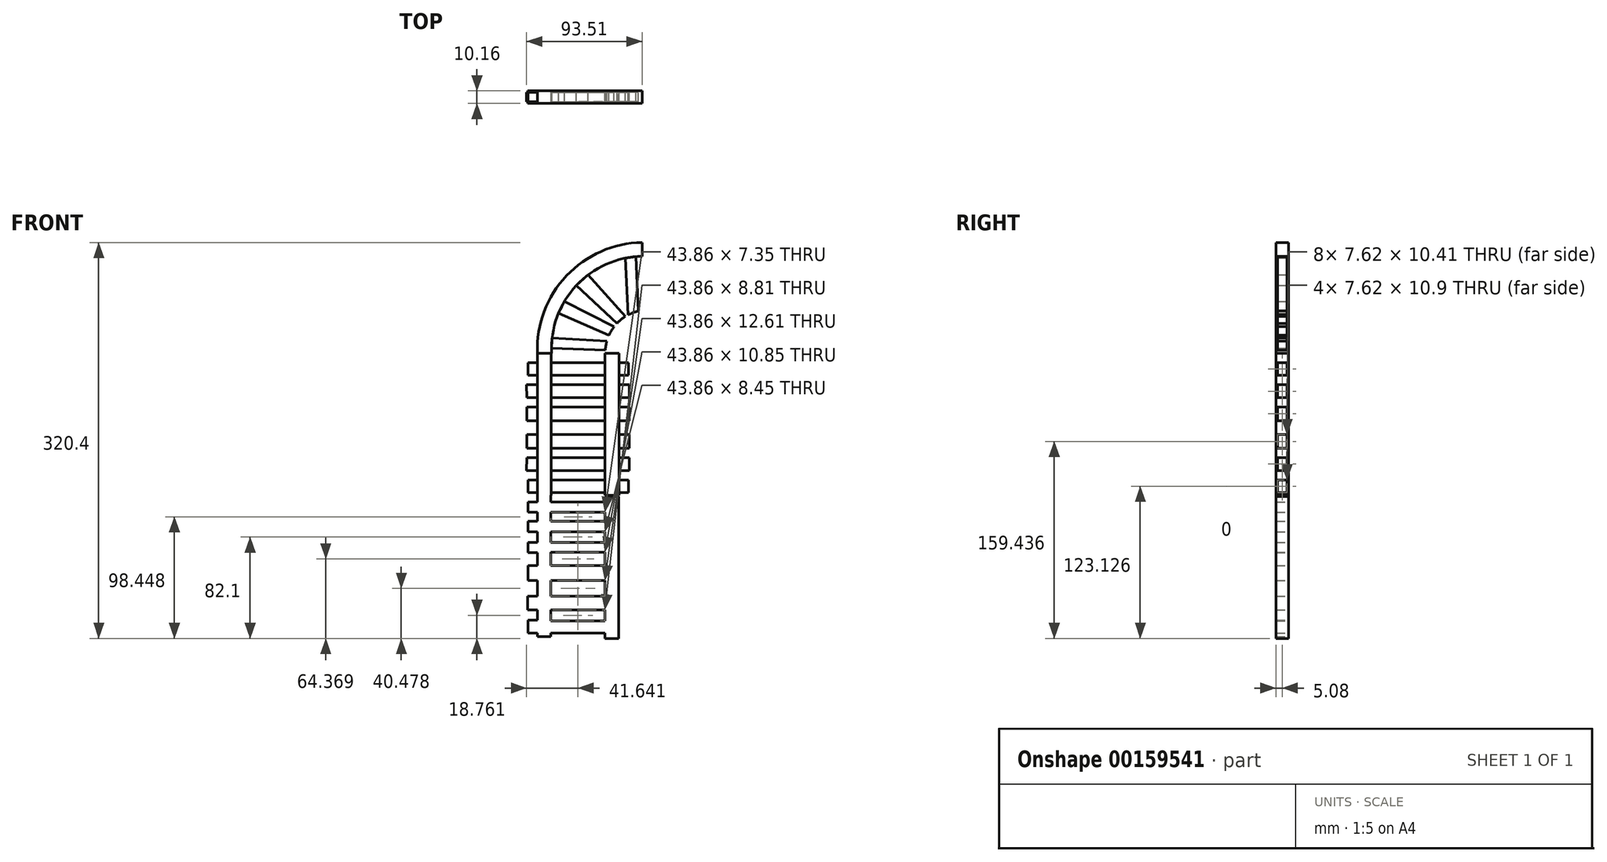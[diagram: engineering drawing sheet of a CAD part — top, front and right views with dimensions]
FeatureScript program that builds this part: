
annotation { "Feature Type Name" : "Feature", "Feature Type Description" : "" }
export const myFeature = defineFeature(function(context is Context, id is Id, definition is map)
    precondition{}
    {
        {
            var Q0;
            Q0=qCreatedBy(makeId("Front.planeOp"),FACE);
            var sketch = newSketch(context, id + "F0", { "sketchPlane" : qUnion([Q0])});
            skLineSegment(sketch, "E0", {"start": v(-21.84, 60.28) * mm, "end": v(-21.84, -54.78) * mm});
            skLineSegment(sketch, "E1", {"start": v(-21.84, -54.78) * mm, "end": v(-33.02, -54.78) * mm});
            skLineSegment(sketch, "E2", {"start": v(-33.02, -54.78) * mm, "end": v(-33.02, 60.28) * mm});
            skLineSegment(sketch, "E3", {"start": v(-33.02, 60.28) * mm, "end": v(-21.84, 60.28) * mm});
            skLineSegment(sketch, "E4.MirrorCS", {"start": v(21.84, 60.28) * mm, "end": v(21.84, -54.78) * mm});
            skLineSegment(sketch, "E5.MirrorCS", {"start": v(33.02, -54.78) * mm, "end": v(33.02, 60.28) * mm});
            skLineSegment(sketch, "E6.MirrorCS", {"start": v(33.02, 60.28) * mm, "end": v(21.84, 60.28) * mm});
            skLineSegment(sketch, "E7.MirrorCS", {"start": v(21.84, -54.78) * mm, "end": v(33.02, -54.78) * mm});
            skLineSegment(sketch, "E8", {"start": v(-40.64, 42.25) * mm, "end": v(40.64, 42.25) * mm});
            skLineSegment(sketch, "E9", {"start": v(40.64, 42.25) * mm, "end": v(40.64, 52.66) * mm});
            skLineSegment(sketch, "E10", {"start": v(40.64, 52.66) * mm, "end": v(-40.64, 52.66) * mm});
            skLineSegment(sketch, "E11", {"start": v(-40.64, 52.66) * mm, "end": v(-40.64, 42.25) * mm});
            skLineSegment(sketch, "E12", {"start": v(-41.74, 34.63) * mm, "end": v(41.35, 34.63) * mm});
            skLineSegment(sketch, "E13", {"start": v(41.35, 34.63) * mm, "end": v(41.35, 24.21) * mm});
            skLineSegment(sketch, "E14", {"start": v(41.35, 24.21) * mm, "end": v(-41.51, 24.21) * mm});
            skLineSegment(sketch, "E15", {"start": v(-41.51, 24.21) * mm, "end": v(-41.74, 34.63) * mm});
            skLineSegment(sketch, "E16", {"start": v(-33.02, 16.6) * mm, "end": v(-41.51, 16.6) * mm});
            skLineSegment(sketch, "E17", {"start": v(-41.51, 16.6) * mm, "end": v(-41.51, 5.7) * mm});
            skLineSegment(sketch, "E18", {"start": v(-41.51, 5.7) * mm, "end": v(41.4, 5.7) * mm});
            skLineSegment(sketch, "E19", {"start": v(41.4, 5.7) * mm, "end": v(41.4, 16.6) * mm});
            skLineSegment(sketch, "E20", {"start": v(-33.02, 16.6) * mm, "end": v(41.4, 16.6) * mm});
            skLineSegment(sketch, "E21.MirrorCS", {"start": v(-41.51, -5.7) * mm, "end": v(41.4, -5.7) * mm});
            skLineSegment(sketch, "E22.MirrorCS", {"start": v(-41.51, -16.6) * mm, "end": v(-41.51, -5.7) * mm});
            skLineSegment(sketch, "E23.MirrorCS", {"start": v(41.4, -5.7) * mm, "end": v(41.4, -16.6) * mm});
            skLineSegment(sketch, "E24.MirrorCS", {"start": v(-33.02, -16.6) * mm, "end": v(41.4, -16.6) * mm});
            skLineSegment(sketch, "E25.MirrorCS", {"start": v(-33.02, -16.6) * mm, "end": v(-41.51, -16.6) * mm});
            skLineSegment(sketch, "E26.MirrorCS", {"start": v(41.35, -24.21) * mm, "end": v(-41.51, -24.21) * mm});
            skLineSegment(sketch, "E27.MirrorCS", {"start": v(-41.74, -34.63) * mm, "end": v(41.35, -34.63) * mm});
            skLineSegment(sketch, "E28.MirrorCS", {"start": v(-41.51, -24.21) * mm, "end": v(-41.74, -34.63) * mm});
            skLineSegment(sketch, "E29.MirrorCS", {"start": v(41.35, -34.63) * mm, "end": v(41.35, -24.21) * mm});
            skLineSegment(sketch, "E30.MirrorCS", {"start": v(40.64, -42.25) * mm, "end": v(40.64, -52.66) * mm});
            skLineSegment(sketch, "E31.MirrorCS", {"start": v(40.64, -52.66) * mm, "end": v(-40.64, -52.66) * mm});
            skLineSegment(sketch, "E32.MirrorCS", {"start": v(-40.64, -42.25) * mm, "end": v(40.64, -42.25) * mm});
            skLineSegment(sketch, "E33.MirrorCS", {"start": v(-40.64, -52.66) * mm, "end": v(-40.64, -42.25) * mm});
            skSolve(sketch);
        }
        {
            var Q0;
            {var subQ0=sQuery(id+"F0.wireOp",EDGE,"E3");Q0=makeQuery(id+"F0.imprint","IMPRINT",FACE,{"disambiguationData":[TD([[makeQuery(id+"F0.imprint","IMPRINT",EDGE,{"derivedFrom":subQ0}),-1.0]])]});}
            var Q1;
            {var subQ0=sQuery(id+"F0.wireOp",EDGE,"E10");var subQ1=sQuery(id+"F0.wireOp",EDGE,"E0");var subQ2=makeQuery(id+"F0.imprint","INTERSECT",VERTEX,{"derivedFrom":[subQ1,subQ0]});Q1=makeQuery(id+"F0.imprint","IMPRINT",FACE,{"disambiguationData":[TD([[makeQuery(id+"F0.imprint","IMPRINT",EDGE,{"disambiguationData":[TD([[subQ2,-1.0]])],"derivedFrom":subQ1}),-1.0]])]});}
            var Q2;
            {var subQ0=sQuery(id+"F0.wireOp",EDGE,"E8");var subQ1=sQuery(id+"F0.wireOp",EDGE,"E0");var subQ2=makeQuery(id+"F0.imprint","INTERSECT",VERTEX,{"derivedFrom":[subQ1,subQ0]});Q2=makeQuery(id+"F0.imprint","IMPRINT",FACE,{"disambiguationData":[TD([[makeQuery(id+"F0.imprint","IMPRINT",EDGE,{"disambiguationData":[TD([[subQ2,-1.0]])],"derivedFrom":subQ1}),-1.0]])]});}
            var Q3;
            {var subQ0=sQuery(id+"F0.wireOp",EDGE,"E12");var subQ1=sQuery(id+"F0.wireOp",EDGE,"E0");var subQ2=makeQuery(id+"F0.imprint","INTERSECT",VERTEX,{"derivedFrom":[subQ1,subQ0]});Q3=makeQuery(id+"F0.imprint","IMPRINT",FACE,{"disambiguationData":[TD([[makeQuery(id+"F0.imprint","IMPRINT",EDGE,{"disambiguationData":[TD([[subQ2,-1.0]])],"derivedFrom":subQ1}),-1.0]])]});}
            var Q4;
            {var subQ0=sQuery(id+"F0.wireOp",EDGE,"E14");var subQ1=sQuery(id+"F0.wireOp",EDGE,"E0");var subQ2=makeQuery(id+"F0.imprint","INTERSECT",VERTEX,{"derivedFrom":[subQ1,subQ0]});Q4=makeQuery(id+"F0.imprint","IMPRINT",FACE,{"disambiguationData":[TD([[makeQuery(id+"F0.imprint","IMPRINT",EDGE,{"disambiguationData":[TD([[subQ2,-1.0]])],"derivedFrom":subQ1}),-1.0]])]});}
            var Q5;
            {var subQ0=sQuery(id+"F0.wireOp",EDGE,"E20");var subQ1=sQuery(id+"F0.wireOp",EDGE,"E0");var subQ2=makeQuery(id+"F0.imprint","INTERSECT",VERTEX,{"derivedFrom":[subQ1,subQ0]});Q5=makeQuery(id+"F0.imprint","IMPRINT",FACE,{"disambiguationData":[TD([[makeQuery(id+"F0.imprint","IMPRINT",EDGE,{"disambiguationData":[TD([[subQ2,-1.0]])],"derivedFrom":subQ1}),-1.0]])]});}
            var Q6;
            {var subQ0=sQuery(id+"F0.wireOp",EDGE,"E18");var subQ1=sQuery(id+"F0.wireOp",EDGE,"E0");var subQ2=makeQuery(id+"F0.imprint","INTERSECT",VERTEX,{"derivedFrom":[subQ1,subQ0]});Q6=makeQuery(id+"F0.imprint","IMPRINT",FACE,{"disambiguationData":[TD([[makeQuery(id+"F0.imprint","IMPRINT",EDGE,{"disambiguationData":[TD([[subQ2,-1.0]])],"derivedFrom":subQ1}),-1.0]])]});}
            var Q7;
            {var subQ0=sQuery(id+"F0.wireOp",EDGE,"E21.MirrorCS");var subQ1=sQuery(id+"F0.wireOp",EDGE,"E0");var subQ2=makeQuery(id+"F0.imprint","INTERSECT",VERTEX,{"derivedFrom":[subQ1,subQ0]});Q7=makeQuery(id+"F0.imprint","IMPRINT",FACE,{"disambiguationData":[TD([[makeQuery(id+"F0.imprint","IMPRINT",EDGE,{"disambiguationData":[TD([[subQ2,-1.0]])],"derivedFrom":subQ1}),-1.0]])]});}
            var Q8;
            {var subQ0=sQuery(id+"F0.wireOp",EDGE,"E24.MirrorCS");var subQ1=sQuery(id+"F0.wireOp",EDGE,"E0");var subQ2=makeQuery(id+"F0.imprint","INTERSECT",VERTEX,{"derivedFrom":[subQ1,subQ0]});Q8=makeQuery(id+"F0.imprint","IMPRINT",FACE,{"disambiguationData":[TD([[makeQuery(id+"F0.imprint","IMPRINT",EDGE,{"disambiguationData":[TD([[subQ2,-1.0]])],"derivedFrom":subQ1}),-1.0]])]});}
            var Q9;
            {var subQ0=sQuery(id+"F0.wireOp",EDGE,"E26.MirrorCS");var subQ1=sQuery(id+"F0.wireOp",EDGE,"E0");var subQ2=makeQuery(id+"F0.imprint","INTERSECT",VERTEX,{"derivedFrom":[subQ1,subQ0]});Q9=makeQuery(id+"F0.imprint","IMPRINT",FACE,{"disambiguationData":[TD([[makeQuery(id+"F0.imprint","IMPRINT",EDGE,{"disambiguationData":[TD([[subQ2,-1.0]])],"derivedFrom":subQ1}),-1.0]])]});}
            var Q10;
            {var subQ0=sQuery(id+"F0.wireOp",EDGE,"E27.MirrorCS");var subQ1=sQuery(id+"F0.wireOp",EDGE,"E0");var subQ2=makeQuery(id+"F0.imprint","INTERSECT",VERTEX,{"derivedFrom":[subQ1,subQ0]});Q10=makeQuery(id+"F0.imprint","IMPRINT",FACE,{"disambiguationData":[TD([[makeQuery(id+"F0.imprint","IMPRINT",EDGE,{"disambiguationData":[TD([[subQ2,-1.0]])],"derivedFrom":subQ1}),-1.0]])]});}
            var Q11;
            {var subQ0=sQuery(id+"F0.wireOp",EDGE,"E31.MirrorCS");var subQ1=sQuery(id+"F0.wireOp",EDGE,"E0");var subQ2=makeQuery(id+"F0.imprint","INTERSECT",VERTEX,{"derivedFrom":[subQ1,subQ0]});Q11=makeQuery(id+"F0.imprint","IMPRINT",FACE,{"disambiguationData":[TD([[makeQuery(id+"F0.imprint","IMPRINT",EDGE,{"disambiguationData":[TD([[subQ2,1.0]])],"derivedFrom":subQ1}),-1.0]])]});}
            var Q12;
            {var subQ0=sQuery(id+"F0.wireOp",EDGE,"E31.MirrorCS");var subQ1=sQuery(id+"F0.wireOp",EDGE,"E4.MirrorCS");var subQ2=makeQuery(id+"F0.imprint","INTERSECT",VERTEX,{"derivedFrom":[subQ1,subQ0]});Q12=makeQuery(id+"F0.imprint","IMPRINT",FACE,{"disambiguationData":[TD([[makeQuery(id+"F0.imprint","IMPRINT",EDGE,{"disambiguationData":[TD([[subQ2,1.0]])],"derivedFrom":subQ1}),1.0]])]});}
            var Q13;
            {var subQ0=sQuery(id+"F0.wireOp",EDGE,"E27.MirrorCS");var subQ1=sQuery(id+"F0.wireOp",EDGE,"E4.MirrorCS");var subQ2=makeQuery(id+"F0.imprint","INTERSECT",VERTEX,{"derivedFrom":[subQ1,subQ0]});Q13=makeQuery(id+"F0.imprint","IMPRINT",FACE,{"disambiguationData":[TD([[makeQuery(id+"F0.imprint","IMPRINT",EDGE,{"disambiguationData":[TD([[subQ2,-1.0]])],"derivedFrom":subQ1}),1.0]])]});}
            var Q14;
            {var subQ0=sQuery(id+"F0.wireOp",EDGE,"E26.MirrorCS");var subQ1=sQuery(id+"F0.wireOp",EDGE,"E4.MirrorCS");var subQ2=makeQuery(id+"F0.imprint","INTERSECT",VERTEX,{"derivedFrom":[subQ1,subQ0]});Q14=makeQuery(id+"F0.imprint","IMPRINT",FACE,{"disambiguationData":[TD([[makeQuery(id+"F0.imprint","IMPRINT",EDGE,{"disambiguationData":[TD([[subQ2,-1.0]])],"derivedFrom":subQ1}),1.0]])]});}
            var Q15;
            {var subQ0=sQuery(id+"F0.wireOp",EDGE,"E24.MirrorCS");var subQ1=sQuery(id+"F0.wireOp",EDGE,"E4.MirrorCS");var subQ2=makeQuery(id+"F0.imprint","INTERSECT",VERTEX,{"derivedFrom":[subQ1,subQ0]});Q15=makeQuery(id+"F0.imprint","IMPRINT",FACE,{"disambiguationData":[TD([[makeQuery(id+"F0.imprint","IMPRINT",EDGE,{"disambiguationData":[TD([[subQ2,-1.0]])],"derivedFrom":subQ1}),1.0]])]});}
            var Q16;
            {var subQ0=sQuery(id+"F0.wireOp",EDGE,"E21.MirrorCS");var subQ1=sQuery(id+"F0.wireOp",EDGE,"E4.MirrorCS");var subQ2=makeQuery(id+"F0.imprint","INTERSECT",VERTEX,{"derivedFrom":[subQ1,subQ0]});Q16=makeQuery(id+"F0.imprint","IMPRINT",FACE,{"disambiguationData":[TD([[makeQuery(id+"F0.imprint","IMPRINT",EDGE,{"disambiguationData":[TD([[subQ2,-1.0]])],"derivedFrom":subQ1}),1.0]])]});}
            var Q17;
            {var subQ0=sQuery(id+"F0.wireOp",EDGE,"E18");var subQ1=sQuery(id+"F0.wireOp",EDGE,"E4.MirrorCS");var subQ2=makeQuery(id+"F0.imprint","INTERSECT",VERTEX,{"derivedFrom":[subQ1,subQ0]});Q17=makeQuery(id+"F0.imprint","IMPRINT",FACE,{"disambiguationData":[TD([[makeQuery(id+"F0.imprint","IMPRINT",EDGE,{"disambiguationData":[TD([[subQ2,-1.0]])],"derivedFrom":subQ1}),1.0]])]});}
            var Q18;
            {var subQ0=sQuery(id+"F0.wireOp",EDGE,"E20");var subQ1=sQuery(id+"F0.wireOp",EDGE,"E4.MirrorCS");var subQ2=makeQuery(id+"F0.imprint","INTERSECT",VERTEX,{"derivedFrom":[subQ1,subQ0]});Q18=makeQuery(id+"F0.imprint","IMPRINT",FACE,{"disambiguationData":[TD([[makeQuery(id+"F0.imprint","IMPRINT",EDGE,{"disambiguationData":[TD([[subQ2,-1.0]])],"derivedFrom":subQ1}),1.0]])]});}
            var Q19;
            {var subQ0=sQuery(id+"F0.wireOp",EDGE,"E14");var subQ1=sQuery(id+"F0.wireOp",EDGE,"E4.MirrorCS");var subQ2=makeQuery(id+"F0.imprint","INTERSECT",VERTEX,{"derivedFrom":[subQ1,subQ0]});Q19=makeQuery(id+"F0.imprint","IMPRINT",FACE,{"disambiguationData":[TD([[makeQuery(id+"F0.imprint","IMPRINT",EDGE,{"disambiguationData":[TD([[subQ2,-1.0]])],"derivedFrom":subQ1}),1.0]])]});}
            var Q20;
            {var subQ0=sQuery(id+"F0.wireOp",EDGE,"E12");var subQ1=sQuery(id+"F0.wireOp",EDGE,"E4.MirrorCS");var subQ2=makeQuery(id+"F0.imprint","INTERSECT",VERTEX,{"derivedFrom":[subQ1,subQ0]});Q20=makeQuery(id+"F0.imprint","IMPRINT",FACE,{"disambiguationData":[TD([[makeQuery(id+"F0.imprint","IMPRINT",EDGE,{"disambiguationData":[TD([[subQ2,-1.0]])],"derivedFrom":subQ1}),1.0]])]});}
            var Q21;
            {var subQ0=sQuery(id+"F0.wireOp",EDGE,"E8");var subQ1=sQuery(id+"F0.wireOp",EDGE,"E4.MirrorCS");var subQ2=makeQuery(id+"F0.imprint","INTERSECT",VERTEX,{"derivedFrom":[subQ1,subQ0]});Q21=makeQuery(id+"F0.imprint","IMPRINT",FACE,{"disambiguationData":[TD([[makeQuery(id+"F0.imprint","IMPRINT",EDGE,{"disambiguationData":[TD([[subQ2,-1.0]])],"derivedFrom":subQ1}),1.0]])]});}
            var Q22;
            {var subQ0=sQuery(id+"F0.wireOp",EDGE,"E10");var subQ1=sQuery(id+"F0.wireOp",EDGE,"E4.MirrorCS");var subQ2=makeQuery(id+"F0.imprint","INTERSECT",VERTEX,{"derivedFrom":[subQ1,subQ0]});Q22=makeQuery(id+"F0.imprint","IMPRINT",FACE,{"disambiguationData":[TD([[makeQuery(id+"F0.imprint","IMPRINT",EDGE,{"disambiguationData":[TD([[subQ2,-1.0]])],"derivedFrom":subQ1}),1.0]])]});}
            var Q23;
            {var subQ0=sQuery(id+"F0.wireOp",EDGE,"E6.MirrorCS");Q23=makeQuery(id+"F0.imprint","IMPRINT",FACE,{"disambiguationData":[TD([[makeQuery(id+"F0.imprint","IMPRINT",EDGE,{"derivedFrom":subQ0}),1.0]])]});}
            var Q24;
            {var subQ0=sQuery(id+"F0.wireOp",EDGE,"E7.MirrorCS");Q24=makeQuery(id+"F0.imprint","IMPRINT",FACE,{"disambiguationData":[TD([[makeQuery(id+"F0.imprint","IMPRINT",EDGE,{"derivedFrom":subQ0}),1.0]])]});}
            var Q25;
            {var subQ0=sQuery(id+"F0.wireOp",EDGE,"E1");Q25=makeQuery(id+"F0.imprint","IMPRINT",FACE,{"disambiguationData":[TD([[makeQuery(id+"F0.imprint","IMPRINT",EDGE,{"derivedFrom":subQ0}),-1.0]])]});}
            extrude(context, id + "F1", {"entities" : qUnion([Q0, Q1, Q2, Q3, Q4, Q5, Q6, Q7, Q8, Q9, Q10, Q11, Q12, Q13, Q14, Q15, Q16, Q17, Q18, Q19, Q20, Q21, Q22, Q23, Q24, Q25]), "depth" : 5.08 * mm, "hasSecondDirection" : true, "secondDirectionOppositeDirection" : true, "secondDirectionDepth" : 5.08 * mm});
        }
        {
            var Q0;
            {var subQ0=sQuery(id+"F0.wireOp",EDGE,"E12");var subQ1=sQuery(id+"F0.wireOp",EDGE,"E0");var subQ2=makeQuery(id+"F0.imprint","INTERSECT",VERTEX,{"derivedFrom":[subQ1,subQ0]});Q0=makeQuery(id+"F0.imprint","IMPRINT",FACE,{"disambiguationData":[TD([[makeQuery(id+"F0.imprint","IMPRINT",EDGE,{"disambiguationData":[TD([[subQ2,-1.0]])],"derivedFrom":subQ1}),1.0]])]});}
            var Q1;
            {var subQ0=sQuery(id+"F0.wireOp",EDGE,"E10");var subQ1=sQuery(id+"F0.wireOp",EDGE,"E0");var subQ2=makeQuery(id+"F0.imprint","INTERSECT",VERTEX,{"derivedFrom":[subQ1,subQ0]});Q1=makeQuery(id+"F0.imprint","IMPRINT",FACE,{"disambiguationData":[TD([[makeQuery(id+"F0.imprint","IMPRINT",EDGE,{"disambiguationData":[TD([[subQ2,-1.0]])],"derivedFrom":subQ1}),1.0]])]});}
            var Q2;
            {var subQ5=sQuery(id+"F0.wireOp",EDGE,"E11");Q2=makeQuery(id+"F0.imprint","IMPRINT",FACE,{"disambiguationData":[TD([[makeQuery(id+"F0.imprint","IMPRINT",EDGE,{"derivedFrom":subQ5}),1.0]])]});}
            var Q3;
            {var subQ5=sQuery(id+"F0.wireOp",EDGE,"E15");Q3=makeQuery(id+"F0.imprint","IMPRINT",FACE,{"disambiguationData":[TD([[makeQuery(id+"F0.imprint","IMPRINT",EDGE,{"derivedFrom":subQ5}),-1.0]])]});}
            var Q4;
            {var subQ0=sQuery(id+"F0.wireOp",EDGE,"E16");Q4=makeQuery(id+"F0.imprint","IMPRINT",FACE,{"disambiguationData":[TD([[makeQuery(id+"F0.imprint","IMPRINT",EDGE,{"derivedFrom":subQ0}),1.0]])]});}
            var Q5;
            {var subQ4=sQuery(id+"F0.wireOp",EDGE,"E22.MirrorCS");Q5=makeQuery(id+"F0.imprint","IMPRINT",FACE,{"disambiguationData":[TD([[makeQuery(id+"F0.imprint","IMPRINT",EDGE,{"derivedFrom":subQ4}),-1.0]])]});}
            var Q6;
            {var subQ0=sQuery(id+"F0.wireOp",EDGE,"E21.MirrorCS");var subQ1=sQuery(id+"F0.wireOp",EDGE,"E0");var subQ2=makeQuery(id+"F0.imprint","INTERSECT",VERTEX,{"derivedFrom":[subQ1,subQ0]});Q6=makeQuery(id+"F0.imprint","IMPRINT",FACE,{"disambiguationData":[TD([[makeQuery(id+"F0.imprint","IMPRINT",EDGE,{"disambiguationData":[TD([[subQ2,-1.0]])],"derivedFrom":subQ1}),1.0]])]});}
            var Q7;
            {var subQ0=sQuery(id+"F0.wireOp",EDGE,"E20");var subQ1=sQuery(id+"F0.wireOp",EDGE,"E0");var subQ2=makeQuery(id+"F0.imprint","INTERSECT",VERTEX,{"derivedFrom":[subQ1,subQ0]});Q7=makeQuery(id+"F0.imprint","IMPRINT",FACE,{"disambiguationData":[TD([[makeQuery(id+"F0.imprint","IMPRINT",EDGE,{"disambiguationData":[TD([[subQ2,-1.0]])],"derivedFrom":subQ1}),1.0]])]});}
            var Q8;
            {var subQ0=sQuery(id+"F0.wireOp",EDGE,"E24.MirrorCS");var subQ1=sQuery(id+"F0.wireOp",EDGE,"E5.MirrorCS");var subQ2=makeQuery(id+"F0.imprint","INTERSECT",VERTEX,{"derivedFrom":[subQ1,subQ0]});Q8=makeQuery(id+"F0.imprint","IMPRINT",FACE,{"disambiguationData":[TD([[makeQuery(id+"F0.imprint","IMPRINT",EDGE,{"disambiguationData":[TD([[subQ2,-1.0]])],"derivedFrom":subQ1}),-1.0]])]});}
            var Q9;
            {var subQ0=sQuery(id+"F0.wireOp",EDGE,"E18");var subQ1=sQuery(id+"F0.wireOp",EDGE,"E5.MirrorCS");var subQ2=makeQuery(id+"F0.imprint","INTERSECT",VERTEX,{"derivedFrom":[subQ1,subQ0]});Q9=makeQuery(id+"F0.imprint","IMPRINT",FACE,{"disambiguationData":[TD([[makeQuery(id+"F0.imprint","IMPRINT",EDGE,{"disambiguationData":[TD([[subQ2,-1.0]])],"derivedFrom":subQ1}),-1.0]])]});}
            var Q10;
            {var subQ5=sQuery(id+"F0.wireOp",EDGE,"E13");Q10=makeQuery(id+"F0.imprint","IMPRINT",FACE,{"disambiguationData":[TD([[makeQuery(id+"F0.imprint","IMPRINT",EDGE,{"derivedFrom":subQ5}),-1.0]])]});}
            var Q11;
            {var subQ5=sQuery(id+"F0.wireOp",EDGE,"E9");Q11=makeQuery(id+"F0.imprint","IMPRINT",FACE,{"disambiguationData":[TD([[makeQuery(id+"F0.imprint","IMPRINT",EDGE,{"derivedFrom":subQ5}),1.0]])]});}
            var Q12;
            {var subQ5=sQuery(id+"F0.wireOp",EDGE,"E29.MirrorCS");Q12=makeQuery(id+"F0.imprint","IMPRINT",FACE,{"disambiguationData":[TD([[makeQuery(id+"F0.imprint","IMPRINT",EDGE,{"derivedFrom":subQ5}),1.0]])]});}
            var Q13;
            {var subQ5=sQuery(id+"F0.wireOp",EDGE,"E30.MirrorCS");Q13=makeQuery(id+"F0.imprint","IMPRINT",FACE,{"disambiguationData":[TD([[makeQuery(id+"F0.imprint","IMPRINT",EDGE,{"derivedFrom":subQ5}),-1.0]])]});}
            var Q14;
            {var subQ0=sQuery(id+"F0.wireOp",EDGE,"E31.MirrorCS");var subQ1=sQuery(id+"F0.wireOp",EDGE,"E0");var subQ2=makeQuery(id+"F0.imprint","INTERSECT",VERTEX,{"derivedFrom":[subQ1,subQ0]});Q14=makeQuery(id+"F0.imprint","IMPRINT",FACE,{"disambiguationData":[TD([[makeQuery(id+"F0.imprint","IMPRINT",EDGE,{"disambiguationData":[TD([[subQ2,1.0]])],"derivedFrom":subQ1}),1.0]])]});}
            var Q15;
            {var subQ0=sQuery(id+"F0.wireOp",EDGE,"E26.MirrorCS");var subQ1=sQuery(id+"F0.wireOp",EDGE,"E0");var subQ2=makeQuery(id+"F0.imprint","INTERSECT",VERTEX,{"derivedFrom":[subQ1,subQ0]});Q15=makeQuery(id+"F0.imprint","IMPRINT",FACE,{"disambiguationData":[TD([[makeQuery(id+"F0.imprint","IMPRINT",EDGE,{"disambiguationData":[TD([[subQ2,-1.0]])],"derivedFrom":subQ1}),1.0]])]});}
            var Q16;
            {var subQ5=sQuery(id+"F0.wireOp",EDGE,"E28.MirrorCS");Q16=makeQuery(id+"F0.imprint","IMPRINT",FACE,{"disambiguationData":[TD([[makeQuery(id+"F0.imprint","IMPRINT",EDGE,{"derivedFrom":subQ5}),1.0]])]});}
            var Q17;
            {var subQ5=sQuery(id+"F0.wireOp",EDGE,"E33.MirrorCS");Q17=makeQuery(id+"F0.imprint","IMPRINT",FACE,{"disambiguationData":[TD([[makeQuery(id+"F0.imprint","IMPRINT",EDGE,{"derivedFrom":subQ5}),-1.0]])]});}
            var Q18;
            Q18=qSketchRegion(id+"F3",true);
            extrude(context, id + "F2", {"entities" : qUnion([Q0, Q1, Q2, Q3, Q4, Q5, Q6, Q7, Q8, Q9, Q10, Q11, Q12, Q13, Q14, Q15, Q16, Q17, Q18]), "operationType" : NewBodyOperationType.ADD, "depth" : 3.8 * mm, "hasSecondDirection" : true, "secondDirectionOppositeDirection" : true, "secondDirectionDepth" : 3.8 * mm});
        }
        {
            var Q0;
            Q0=qCreatedBy(makeId("Front.planeOp"),FACE);
            var sketch = newSketch(context, id + "F3", { "sketchPlane" : qUnion([Q0])});
            skLineSegment(sketch, "E34", {"start": v(51.77, 83.78) * mm, "end": v(51.77, 149.82) * mm});
            skArc(sketch, "E35", {"start": v(51.77, 149.82) * mm, "mid": v(-9.44, 122.88) * mm, "end": v(-32.96, 60.28) * mm});
            skLineSegment(sketch, "E36", {"start": v(51.77, 149.82) * mm, "end": v(51.77, 138.64) * mm});
            skLineSegment(sketch, "E37", {"start": v(51.77, 83.78) * mm, "end": v(51.77, 94.95) * mm});
            skArc(sketch, "E38", {"start": v(51.77, 138.64) * mm, "mid": v(-1.44, 114.97) * mm, "end": v(-21.43, 60.28) * mm});
            skArc(sketch, "E39", {"start": v(51.77, 83.78) * mm, "mid": v(37.26, 76.12) * mm, "end": v(33.02, 60.28) * mm});
            skArc(sketch, "E40", {"start": v(51.77, 94.95) * mm, "mid": v(25, 74.7) * mm, "end": v(27.58, 41.24) * mm});
            skLineSegment(sketch, "E41", {"start": v(-21.52, 64.26) * mm, "end": v(21.98, 62.59) * mm});
            skLineSegment(sketch, "E42", {"start": v(-21.06, 72.4) * mm, "end": v(23.24, 69.9) * mm});
            skLineSegment(sketch, "E43", {"start": v(-15.86, 92.57) * mm, "end": v(25, 74.7) * mm});
            skLineSegment(sketch, "E44", {"start": v(-11.13, 102.04) * mm, "end": v(29.15, 81.66) * mm});
            skLineSegment(sketch, "E45", {"start": v(33.02, 60.28) * mm, "end": v(21.9, 60.28) * mm});
            skLineSegment(sketch, "E46", {"start": v(-21.43, 60.28) * mm, "end": v(-32.96, 60.28) * mm});
            skLineSegment(sketch, "E47", {"start": v(48.84, 94.4) * mm, "end": v(46.72, 138.38) * mm});
            skLineSegment(sketch, "E48", {"start": v(31.4, 84.31) * mm, "end": v(-1.44, 114.97) * mm});
            skLineSegment(sketch, "E49", {"start": v(8.07, 123.54) * mm, "end": v(38.2, 89.91) * mm});
            skLineSegment(sketch, "E50", {"start": v(40.54, 91.27) * mm, "end": v(38.33, 137.18) * mm});
            skLineSegment(sketch, "E51", {"start": v(21.98, 62.59) * mm, "end": v(23.24, 69.9) * mm});
            skLineSegment(sketch, "E52", {"start": v(-21.06, 72.4) * mm, "end": v(-21.52, 64.26) * mm});
            skLineSegment(sketch, "E53", {"start": v(-11.13, 102.04) * mm, "end": v(-15.86, 92.57) * mm});
            skLineSegment(sketch, "E54", {"start": v(29.15, 81.66) * mm, "end": v(25, 74.7) * mm});
            skLineSegment(sketch, "E55", {"start": v(31.4, 84.31) * mm, "end": v(38.2, 89.91) * mm});
            skLineSegment(sketch, "E56", {"start": v(8.07, 123.54) * mm, "end": v(-1.44, 114.97) * mm});
            skLineSegment(sketch, "E57", {"start": v(38.33, 137.18) * mm, "end": v(46.72, 138.38) * mm});
            skLineSegment(sketch, "E58", {"start": v(40.54, 91.27) * mm, "end": v(48.84, 94.4) * mm});
            skSolve(sketch);
        }
        {
            var Q0;
            Q0=makeQuery(id+"F3.imprint","IMPRINT",FACE,{"disambiguationData":[TD([[makeQuery(id+"F3.imprint","IMPRINT",EDGE,{"derivedFrom":sQuery(id+"F3.wireOp",EDGE,"E35")}),1.0]])]});
            var Q1;
            {var subQ5=sQuery(id+"F3.wireOp",EDGE,"E37");Q1=makeQuery(id+"F3.imprint","IMPRINT",FACE,{"disambiguationData":[TD([[makeQuery(id+"F3.imprint","IMPRINT",EDGE,{"derivedFrom":subQ5}),1.0]])]});}
            extrude(context, id + "F4", {"entities" : qUnion([Q0, Q1]), "depth" : 5.08 * mm, "hasSecondDirection" : true, "secondDirectionOppositeDirection" : true, "secondDirectionDepth" : 5.08 * mm});
        }
        {
            var Q0;
            {var subQ1=sQuery(id+"F3.wireOp",EDGE,"E41");Q0=makeQuery(id+"F3.imprint","IMPRINT",FACE,{"disambiguationData":[TD([[makeQuery(id+"F3.imprint","IMPRINT",EDGE,{"derivedFrom":subQ1}),1.0]])]});}
            var Q1;
            {var subQ1=sQuery(id+"F3.wireOp",EDGE,"E43");Q1=makeQuery(id+"F3.imprint","IMPRINT",FACE,{"disambiguationData":[TD([[makeQuery(id+"F3.imprint","IMPRINT",EDGE,{"derivedFrom":subQ1}),1.0]])]});}
            var Q2;
            {var subQ1=sQuery(id+"F3.wireOp",EDGE,"E48");Q2=makeQuery(id+"F3.imprint","IMPRINT",FACE,{"disambiguationData":[TD([[makeQuery(id+"F3.imprint","IMPRINT",EDGE,{"derivedFrom":subQ1}),-1.0]])]});}
            var Q3;
            {var subQ1=sQuery(id+"F3.wireOp",EDGE,"E47");Q3=makeQuery(id+"F3.imprint","IMPRINT",FACE,{"disambiguationData":[TD([[makeQuery(id+"F3.imprint","IMPRINT",EDGE,{"derivedFrom":subQ1}),1.0]])]});}
            extrude(context, id + "F5", {"entities" : qUnion([Q0, Q1, Q2, Q3]), "operationType" : NewBodyOperationType.ADD, "depth" : 3.8 * mm, "hasSecondDirection" : true, "secondDirectionOppositeDirection" : true, "secondDirectionDepth" : 3.8 * mm});
        }
        {
            var Q0;
            Q0=makeQuery(id+"F1.opExtrude","CAP_FACE",FACE,{"disambiguationData":[OSD([sQuery(id+"F0.wireOp",EDGE,"E4.MirrorCS"),sQuery(id+"F0.wireOp",EDGE,"E5.MirrorCS"),sQuery(id+"F0.wireOp",EDGE,"E6.MirrorCS"),sQuery(id+"F0.wireOp",EDGE,"E7.MirrorCS")])],"isStart":false});
            var sketch = newSketch(context, id + "F6", { "sketchPlane" : qUnion([Q0])});
            skSolve(sketch);
        }
        {
            var Q0;
            Q0=qCreatedBy(makeId("Front.planeOp"),FACE);
            var sketch = newSketch(context, id + "F7", { "sketchPlane" : qUnion([Q0])});
            skLineSegment(sketch, "E59", {"start": v(-32.94, -54.23) * mm, "end": v(-32.94, -169.04) * mm});
            skLineSegment(sketch, "E60", {"start": v(-32.94, -54.23) * mm, "end": v(-22.03, -54.23) * mm});
            skLineSegment(sketch, "E61", {"start": v(-22.03, -54.23) * mm, "end": v(-22.03, -169.04) * mm});
            skLineSegment(sketch, "E62", {"start": v(-22.03, -169.04) * mm, "end": v(-32.94, -169.04) * mm});
            skLineSegment(sketch, "E63", {"start": v(21.83, -170.58) * mm, "end": v(32.85, -170.58) * mm});
            skLineSegment(sketch, "E64", {"start": v(-32.94, -60) * mm, "end": v(-40.62, -60) * mm});
            skLineSegment(sketch, "E65", {"start": v(-40.62, -60) * mm, "end": v(-40.62, -68.46) * mm});
            skLineSegment(sketch, "E66", {"start": v(-40.62, -68.46) * mm, "end": v(-32.94, -68.46) * mm});
            skLineSegment(sketch, "E67", {"start": v(-22.03, -60) * mm, "end": v(21.83, -60) * mm});
            skLineSegment(sketch, "E68", {"start": v(-22.03, -68.46) * mm, "end": v(21.83, -68.46) * mm});
            skLineSegment(sketch, "E69", {"start": v(32.85, -60) * mm, "end": v(40.57, -60) * mm});
            skLineSegment(sketch, "E70", {"start": v(40.57, -60) * mm, "end": v(40.57, -68.46) * mm});
            skLineSegment(sketch, "E71", {"start": v(40.57, -68.46) * mm, "end": v(32.85, -68.46) * mm});
            skLineSegment(sketch, "E72", {"start": v(-32.94, -75.8) * mm, "end": v(-40.62, -75.8) * mm});
            skLineSegment(sketch, "E73", {"start": v(-40.62, -75.8) * mm, "end": v(-40.62, -84.26) * mm});
            skLineSegment(sketch, "E74", {"start": v(-40.62, -84.26) * mm, "end": v(-32.94, -84.26) * mm});
            skLineSegment(sketch, "E75", {"start": v(21.83, -84.26) * mm, "end": v(-22.03, -84.26) * mm});
            skLineSegment(sketch, "E76", {"start": v(-22.03, -75.8) * mm, "end": v(21.83, -75.8) * mm});
            skLineSegment(sketch, "E77", {"start": v(32.85, -75.8) * mm, "end": v(40.57, -75.8) * mm});
            skLineSegment(sketch, "E78", {"start": v(40.57, -75.8) * mm, "end": v(40.57, -84.26) * mm});
            skLineSegment(sketch, "E79", {"start": v(40.57, -84.26) * mm, "end": v(32.85, -84.26) * mm});
            skLineSegment(sketch, "E80", {"start": v(-40.62, -92.7) * mm, "end": v(-32.94, -92.7) * mm});
            skLineSegment(sketch, "E81", {"start": v(-40.62, -92.7) * mm, "end": v(-40.62, -101.15) * mm});
            skLineSegment(sketch, "E82", {"start": v(-40.62, -101.15) * mm, "end": v(-32.94, -101.15) * mm});
            skLineSegment(sketch, "E83", {"start": v(-22.03, -92.7) * mm, "end": v(21.83, -92.7) * mm});
            skLineSegment(sketch, "E84", {"start": v(-22.03, -100.79) * mm, "end": v(21.83, -100.79) * mm});
            skLineSegment(sketch, "E85", {"start": v(32.85, -91.97) * mm, "end": v(40.93, -91.97) * mm});
            skLineSegment(sketch, "E86", {"start": v(40.93, -91.97) * mm, "end": v(40.93, -100.42) * mm});
            skLineSegment(sketch, "E87", {"start": v(40.93, -100.42) * mm, "end": v(32.85, -100.42) * mm});
            skLineSegment(sketch, "E88", {"start": v(-22.03, -111.64) * mm, "end": v(21.83, -111.64) * mm});
            skLineSegment(sketch, "E89", {"start": v(21.83, -111.64) * mm, "end": v(21.83, -123.8) * mm});
            skLineSegment(sketch, "E90", {"start": v(21.83, -123.8) * mm, "end": v(-22.03, -123.8) * mm});
            skLineSegment(sketch, "E91", {"start": v(-32.94, -111.64) * mm, "end": v(-40.4, -111.64) * mm});
            skLineSegment(sketch, "E92", {"start": v(-40.4, -111.64) * mm, "end": v(-40.4, -123.8) * mm});
            skLineSegment(sketch, "E93", {"start": v(-40.4, -123.8) * mm, "end": v(-32.94, -123.8) * mm});
            skLineSegment(sketch, "E94", {"start": v(32.85, -113.28) * mm, "end": v(41.25, -113.28) * mm});
            skLineSegment(sketch, "E95", {"start": v(41.25, -113.28) * mm, "end": v(41.25, -124.38) * mm});
            skLineSegment(sketch, "E96", {"start": v(41.25, -124.38) * mm, "end": v(32.85, -124.38) * mm});
            skLineSegment(sketch, "E97", {"start": v(-22.03, -136.4) * mm, "end": v(21.83, -136.4) * mm});
            skLineSegment(sketch, "E98", {"start": v(21.83, -136.4) * mm, "end": v(21.83, -147.42) * mm});
            skLineSegment(sketch, "E99", {"start": v(21.83, -147.42) * mm, "end": v(-22.03, -147.42) * mm});
            skLineSegment(sketch, "E100", {"start": v(-32.94, -136.4) * mm, "end": v(-40.73, -136.4) * mm});
            skLineSegment(sketch, "E101", {"start": v(-32.94, -147.42) * mm, "end": v(-40.73, -147.42) * mm});
            skLineSegment(sketch, "E102", {"start": v(-40.73, -147.42) * mm, "end": v(-40.73, -136.4) * mm});
            skLineSegment(sketch, "E103", {"start": v(32.85, -136.96) * mm, "end": v(42.94, -136.96) * mm});
            skLineSegment(sketch, "E104", {"start": v(42.94, -136.96) * mm, "end": v(42.94, -148.52) * mm});
            skLineSegment(sketch, "E105", {"start": v(42.94, -148.52) * mm, "end": v(32.85, -148.52) * mm});
            skLineSegment(sketch, "E106", {"start": v(-32.94, -155.67) * mm, "end": v(-40.4, -155.67) * mm});
            skPoint(sketch, "E106.endSnap0", {"position": v(-40.4, -117.72) * mm});
            skLineSegment(sketch, "E107", {"start": v(-40.4, -155.67) * mm, "end": v(-40.4, -166.13) * mm});
            skLineSegment(sketch, "E108", {"start": v(-40.4, -166.13) * mm, "end": v(-32.94, -166.13) * mm});
            skLineSegment(sketch, "E109", {"start": v(-22.03, -156.22) * mm, "end": v(21.83, -156.22) * mm});
            skLineSegment(sketch, "E110", {"start": v(21.83, -55.6) * mm, "end": v(21.83, -170.58) * mm});
            skLineSegment(sketch, "E111", {"start": v(21.83, -55.6) * mm, "end": v(32.78, -55.6) * mm});
            skLineSegment(sketch, "E112", {"start": v(32.78, -55.6) * mm, "end": v(32.85, -170.58) * mm});
            skLineSegment(sketch, "E113", {"start": v(-22.03, -166.1) * mm, "end": v(21.83, -166.1) * mm});
            skLineSegment(sketch, "E114", {"start": v(32.84, -156.22) * mm, "end": v(43.17, -156.22) * mm});
            skLineSegment(sketch, "E115", {"start": v(43.17, -156.22) * mm, "end": v(43.18, -166.87) * mm});
            skLineSegment(sketch, "E116", {"start": v(43.18, -166.87) * mm, "end": v(32.85, -166.88) * mm});
            skSolve(sketch);
        }
        {
            var Q0;
            {var subQ0=sQuery(id+"F7.wireOp",EDGE,"E67");Q0=makeQuery(id+"F7.imprint","IMPRINT",FACE,{"disambiguationData":[TD([[makeQuery(id+"F7.imprint","IMPRINT",EDGE,{"derivedFrom":subQ0}),-1.0]])]});}
            var Q1;
            {var subQ3=sQuery(id+"F7.wireOp",EDGE,"E60");Q1=makeQuery(id+"F7.imprint","IMPRINT",FACE,{"disambiguationData":[TD([[makeQuery(id+"F7.imprint","IMPRINT",EDGE,{"derivedFrom":subQ3}),-1.0]])]});}
            var Q2;
            {var subQ0=sQuery(id+"F7.wireOp",EDGE,"E64");Q2=makeQuery(id+"F7.imprint","IMPRINT",FACE,{"disambiguationData":[TD([[makeQuery(id+"F7.imprint","IMPRINT",EDGE,{"derivedFrom":subQ0}),1.0]])]});}
            var Q3;
            {var subQ0=sQuery(id+"F7.wireOp",EDGE,"E72");Q3=makeQuery(id+"F7.imprint","IMPRINT",FACE,{"disambiguationData":[TD([[makeQuery(id+"F7.imprint","IMPRINT",EDGE,{"derivedFrom":subQ0}),1.0]])]});}
            var Q4;
            {var subQ0=sQuery(id+"F7.wireOp",EDGE,"E80");Q4=makeQuery(id+"F7.imprint","IMPRINT",FACE,{"disambiguationData":[TD([[makeQuery(id+"F7.imprint","IMPRINT",EDGE,{"derivedFrom":subQ0}),-1.0]])]});}
            var Q5;
            {var subQ0=sQuery(id+"F7.wireOp",EDGE,"E91");Q5=makeQuery(id+"F7.imprint","IMPRINT",FACE,{"disambiguationData":[TD([[makeQuery(id+"F7.imprint","IMPRINT",EDGE,{"derivedFrom":subQ0}),1.0]])]});}
            var Q6;
            {var subQ0=sQuery(id+"F7.wireOp",EDGE,"E100");Q6=makeQuery(id+"F7.imprint","IMPRINT",FACE,{"disambiguationData":[TD([[makeQuery(id+"F7.imprint","IMPRINT",EDGE,{"derivedFrom":subQ0}),1.0]])]});}
            var Q7;
            {var subQ0=sQuery(id+"F7.wireOp",EDGE,"E106");Q7=makeQuery(id+"F7.imprint","IMPRINT",FACE,{"disambiguationData":[TD([[makeQuery(id+"F7.imprint","IMPRINT",EDGE,{"derivedFrom":subQ0}),1.0]])]});}
            var Q8;
            {var subQ0=sQuery(id+"F7.wireOp",EDGE,"E109");Q8=makeQuery(id+"F7.imprint","IMPRINT",FACE,{"disambiguationData":[TD([[makeQuery(id+"F7.imprint","IMPRINT",EDGE,{"derivedFrom":subQ0}),-1.0]])]});}
            var Q9;
            {var subQ0=sQuery(id+"F7.wireOp",EDGE,"E97");Q9=makeQuery(id+"F7.imprint","IMPRINT",FACE,{"disambiguationData":[TD([[makeQuery(id+"F7.imprint","IMPRINT",EDGE,{"derivedFrom":subQ0}),-1.0]])]});}
            var Q10;
            {var subQ0=sQuery(id+"F7.wireOp",EDGE,"E88");Q10=makeQuery(id+"F7.imprint","IMPRINT",FACE,{"disambiguationData":[TD([[makeQuery(id+"F7.imprint","IMPRINT",EDGE,{"derivedFrom":subQ0}),-1.0]])]});}
            var Q11;
            {var subQ0=sQuery(id+"F7.wireOp",EDGE,"E83");Q11=makeQuery(id+"F7.imprint","IMPRINT",FACE,{"disambiguationData":[TD([[makeQuery(id+"F7.imprint","IMPRINT",EDGE,{"derivedFrom":subQ0}),-1.0]])]});}
            var Q12;
            {var subQ0=sQuery(id+"F7.wireOp",EDGE,"E75");Q12=makeQuery(id+"F7.imprint","IMPRINT",FACE,{"disambiguationData":[TD([[makeQuery(id+"F7.imprint","IMPRINT",EDGE,{"derivedFrom":subQ0}),-1.0]])]});}
            var Q13;
            {var subQ10=sQuery(id+"F7.wireOp",EDGE,"E63");Q13=makeQuery(id+"F7.imprint","IMPRINT",FACE,{"disambiguationData":[TD([[makeQuery(id+"F7.imprint","IMPRINT",EDGE,{"derivedFrom":subQ10}),1.0]])]});}
            extrude(context, id + "F8", {"entities" : qUnion([Q0, Q1, Q2, Q3, Q4, Q5, Q6, Q7, Q8, Q9, Q10, Q11, Q12, Q13]), "operationType" : NewBodyOperationType.ADD, "endBound" : BoundingType.SYMMETRIC, "depth" : 10.16 * mm});
        }
    });
